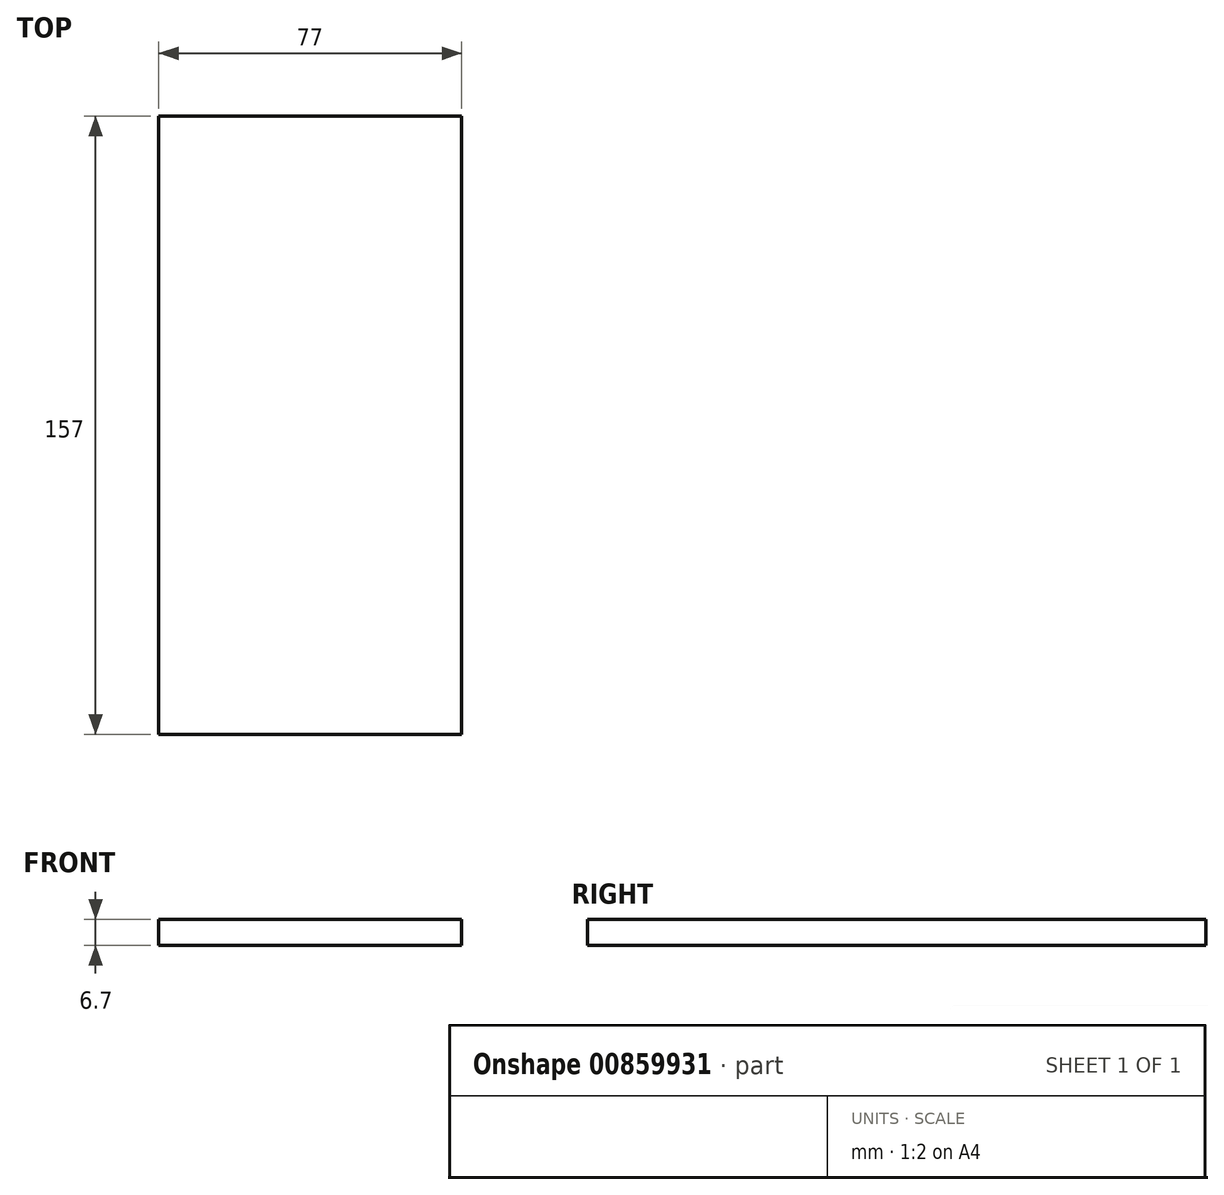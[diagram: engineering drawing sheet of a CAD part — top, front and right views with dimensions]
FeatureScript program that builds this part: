
annotation { "Feature Type Name" : "Feature", "Feature Type Description" : "" }
export const myFeature = defineFeature(function(context is Context, id is Id, definition is map)
    precondition{}
    {
        {
            var Q0;
            Q0=qCreatedBy(makeId("Top.planeOp"),FACE);
            var sketch = newSketch(context, id + "F0", { "sketchPlane" : qUnion([Q0])});
            skLineSegment(sketch, "E0.bottom", {"start": v(-39.2, 71.26) * mm, "end": v(37.8, 71.26) * mm});
            skLineSegment(sketch, "E0.top", {"start": v(-39.2, -85.74) * mm, "end": v(37.8, -85.74) * mm});
            skLineSegment(sketch, "E0.left", {"start": v(-39.2, 71.26) * mm, "end": v(-39.2, -85.74) * mm});
            skLineSegment(sketch, "E0.right", {"start": v(37.8, 71.26) * mm, "end": v(37.8, -85.74) * mm});
            skLineSegment(sketch, "E1", {"start": v(-39.2, 71.26) * mm, "end": v(-39.2, 52.86) * mm});
            skLineSegment(sketch, "E2", {"start": v(-39.2, 52.86) * mm, "end": v(-39.2, 49.78) * mm});
            skLineSegment(sketch, "E3", {"start": v(-39.2, 49.78) * mm, "end": v(-39.2, 34.48) * mm});
            skLineSegment(sketch, "E4", {"start": v(-39.2, 34.48) * mm, "end": v(-39.2, 25.88) * mm});
            skLineSegment(sketch, "E5", {"start": v(-39.2, 25.88) * mm, "end": v(-39.2, 12.93) * mm});
            skSolve(sketch);
        }
        {
            var Q0;
            Q0 = qSketchRegion(id + "F0", true);
            extrude(context, id + "F1", {"entities" : qUnion([Q0]), "depth" : 6.7 * mm, "offsetDistance" : 25 * mm});
        }
    });
